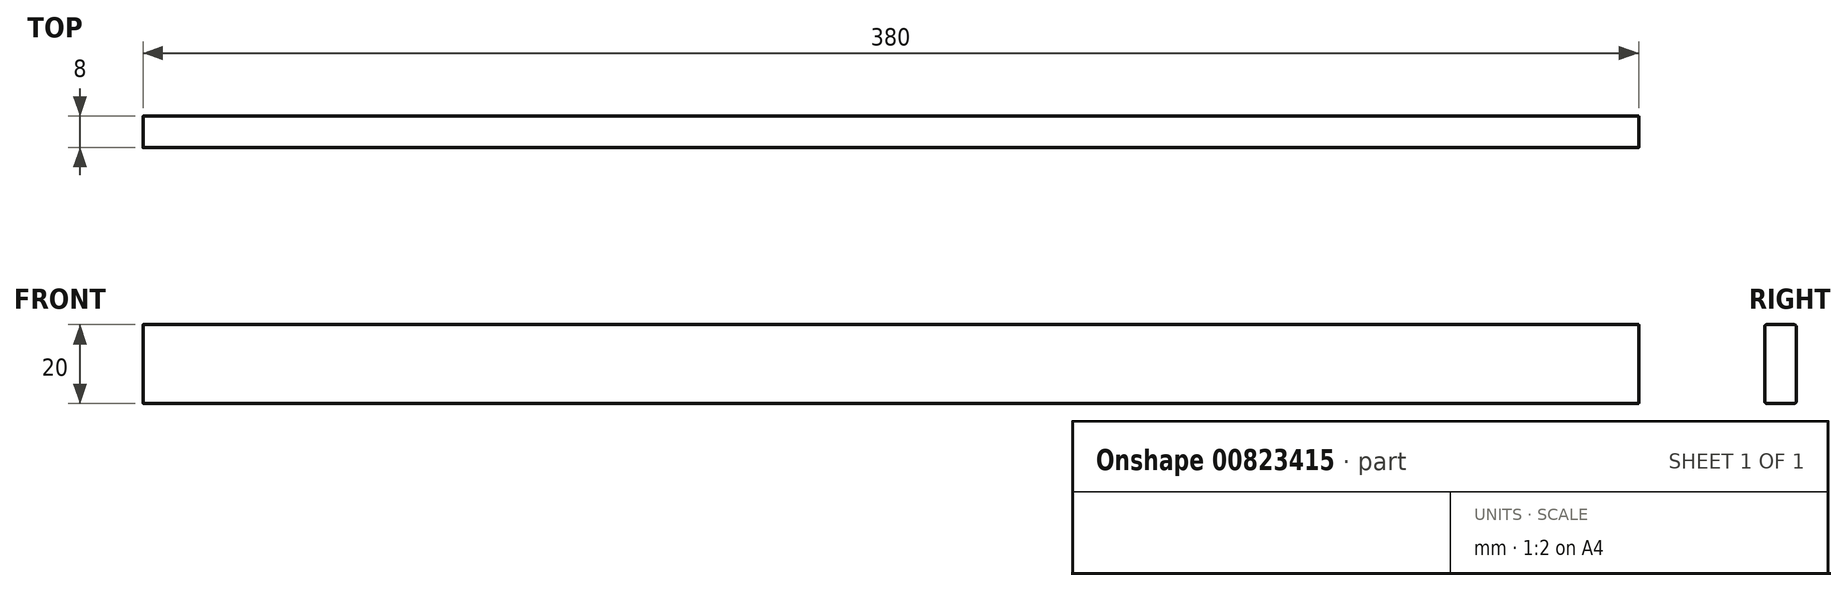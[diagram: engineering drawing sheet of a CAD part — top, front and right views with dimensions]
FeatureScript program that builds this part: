
annotation { "Feature Type Name" : "Feature", "Feature Type Description" : "" }
export const myFeature = defineFeature(function(context is Context, id is Id, definition is map)
    precondition{}
    {
        {
            var Q0;
            Q0=qCreatedBy(makeId("Front.planeOp"),FACE);
            var sketch = newSketch(context, id + "F0", { "sketchPlane" : qUnion([Q0])});
            skLineSegment(sketch, "E0.bottom", {"start": v(-190, 10) * mm, "end": v(190, 10) * mm});
            skLineSegment(sketch, "E0.top", {"start": v(-190, -10) * mm, "end": v(190, -10) * mm});
            skLineSegment(sketch, "E0.left", {"start": v(-190, 10) * mm, "end": v(-190, -10) * mm});
            skLineSegment(sketch, "E0.right", {"start": v(190, 10) * mm, "end": v(190, -10) * mm});
            skPoint(sketch, "E0.middle", {"position": v(0, 0) * mm});
            skSolve(sketch);
        }
        {
            var Q0;
            Q0=makeQuery(id+"F0.imprint","IMPRINT",FACE,{"disambiguationData":[TD([[makeQuery(id+"F0.imprint","IMPRINT",EDGE,{"derivedFrom":sQuery(id+"F0.wireOp",EDGE,"E0.bottom")}),-1.0]])]});
            extrude(context, id + "F1", {"entities" : qUnion([Q0]), "depth" : 8 * mm, "offsetDistance" : 25 * mm});
        }
        {
            var Q0;
            Q0=makeQuery(id+"F1.opExtrude","CAP_EDGE",EDGE,{"disambiguationData":[OSD([sQuery(id+"F0.wireOp",EDGE,"E0.bottom")])],"isStart":false});
            var Q1;
            Q1=makeQuery(id+"F1.opExtrude","CAP_EDGE",EDGE,{"disambiguationData":[OSD([sQuery(id+"F0.wireOp",EDGE,"E0.bottom")])],"isStart":true});
            var Q2;
            Q2=makeQuery(id+"F1.opExtrude","CAP_EDGE",EDGE,{"disambiguationData":[OSD([sQuery(id+"F0.wireOp",EDGE,"E0.top")])],"isStart":true});
            var Q3;
            Q3=makeQuery(id+"F1.opExtrude","CAP_EDGE",EDGE,{"disambiguationData":[OSD([sQuery(id+"F0.wireOp",EDGE,"E0.top")])],"isStart":false});
            fillet(context, id + "F2", {"entities" : qUnion([Q0, Q1, Q2, Q3]), "radius" : 0.5 * mm, "tangentPropagation" : true, "allowEdgeOverflow" : false});
        }
    });
